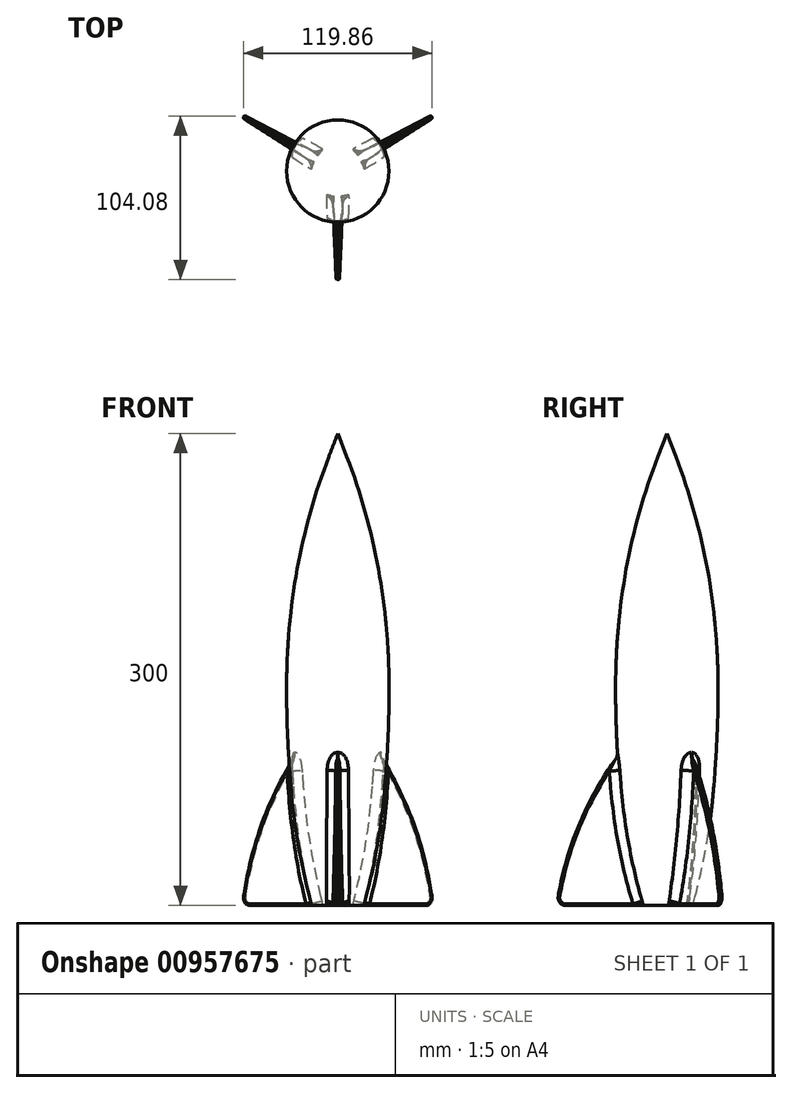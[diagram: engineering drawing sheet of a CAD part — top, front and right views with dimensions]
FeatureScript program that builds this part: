
annotation { "Feature Type Name" : "Feature", "Feature Type Description" : "" }
export const myFeature = defineFeature(function(context is Context, id is Id, definition is map)
    precondition{}
    {
        {
            var Q0;
            Q0=qCreatedBy(makeId("Front.planeOp"),FACE);
            var sketch = newSketch(context, id + "F0", { "sketchPlane" : qUnion([Q0])});
            skLineSegment(sketch, "E0", {"start": v(0, 150) * mm, "end": v(5.68, 135.23) * mm});
            skLineSegment(sketch, "E1", {"start": v(30.36, 31.44) * mm, "end": v(30.51, 29.85) * mm});
            skLineSegment(sketch, "E2", {"start": v(32.5, -9.95) * mm, "end": v(32.5, -14.5) * mm});
            skLineSegment(sketch, "E3", {"start": v(30.5, -65.42) * mm, "end": v(29.8, -74.36) * mm});
            skLineSegment(sketch, "E4", {"start": v(17.92, -144.58) * mm, "end": v(16.5, -150) * mm});
            skLineSegment(sketch, "E5", {"start": v(16.5, -150) * mm, "end": v(0, -150) * mm});
            skLineSegment(sketch, "E6", {"start": v(0, -150) * mm, "end": v(0, 150) * mm});
            skPoint(sketch, "E7.visualSharp", {"position": v(32.5, 10) * mm});
            skArc(sketch, "E7.filletArc", {"start": v(32.5, -9.95) * mm, "mid": v(32, 9.98) * mm, "end": v(30.51, 29.85) * mm});
            skPoint(sketch, "E8.visualSharp", {"position": v(27, -110) * mm});
            skArc(sketch, "E8.filletArc", {"start": v(17.92, -144.58) * mm, "mid": v(25.43, -109.73) * mm, "end": v(29.8, -74.36) * mm});
            skPoint(sketch, "E9.visualSharp", {"position": v(32.5, -40) * mm});
            skArc(sketch, "E9.filletArc", {"start": v(30.5, -65.42) * mm, "mid": v(32, -39.98) * mm, "end": v(32.5, -14.5) * mm});
            skPoint(sketch, "E10.visualSharp", {"position": v(25, 85) * mm});
            skArc(sketch, "E10.filletArc", {"start": v(30.36, 31.44) * mm, "mid": v(21.5, 84.17) * mm, "end": v(5.68, 135.23) * mm});
            skSolve(sketch);
        }
        {
            var Q0;
            Q0=makeQuery(id+"F0.imprint","IMPRINT",FACE,{"disambiguationData":[TD([[makeQuery(id+"F0.imprint","IMPRINT",EDGE,{"derivedFrom":sQuery(id+"F0.wireOp",EDGE,"E0")}),-1.0]])]});
            var Q1;
            Q1=sQuery(id+"F0.wireOp",EDGE,"E6");
            revolve(context, id + "F1", {"surfaceOperationType" : NewSurfaceOperationType.NEW, "entities" : qUnion([Q0]), "axis" : qUnion([Q1]), "revolveType" : RevolveType.FULL});
        }
        {
            var Q0;
            Q0=qCreatedBy(makeId("Top.planeOp"),FACE);
            cPlane(context, id + "F2", {"entities" : qUnion([Q0]), "cplaneType" : CPlaneType.OFFSET, "offset" : 55 * mm, "oppositeDirection" : true, "width" : 150 * mm, "height" : 150 * mm});
        }
        {
            var Q0;
            Q0=qCreatedBy(id+"F2.planeOp",FACE);
            var sketch = newSketch(context, id + "F3", { "sketchPlane" : qUnion([Q0])});
            skLineSegment(sketch, "E11", {"start": v(-1.5, -13) * mm, "end": v(-1, -53) * mm});
            skLineSegment(sketch, "E12", {"start": v(-1, -53) * mm, "end": v(1, -53) * mm});
            skLineSegment(sketch, "E13", {"start": v(1, -53) * mm, "end": v(1.5, -13) * mm});
            skLineSegment(sketch, "E14", {"start": v(1.5, -13) * mm, "end": v(-1.5, -13) * mm});
            skLineSegment(sketch, "E15.1.0", {"start": v(45.4, 27.37) * mm, "end": v(10.5, 7.8) * mm});
            skLineSegment(sketch, "E15.1.1", {"start": v(12, 5.2) * mm, "end": v(46.4, 25.63) * mm});
            skLineSegment(sketch, "E15.1.2", {"start": v(10.5, 7.8) * mm, "end": v(12, 5.2) * mm});
            skLineSegment(sketch, "E15.1.3", {"start": v(46.4, 25.63) * mm, "end": v(45.4, 27.37) * mm});
            skLineSegment(sketch, "E15.2.0", {"start": v(-46.4, 25.63) * mm, "end": v(-12, 5.2) * mm});
            skLineSegment(sketch, "E15.2.1", {"start": v(-10.5, 7.8) * mm, "end": v(-45.4, 27.37) * mm});
            skLineSegment(sketch, "E15.2.2", {"start": v(-12, 5.2) * mm, "end": v(-10.5, 7.8) * mm});
            skLineSegment(sketch, "E15.2.3", {"start": v(-45.4, 27.37) * mm, "end": v(-46.4, 25.63) * mm});
            skPoint(sketch, "E15.center", {"position": v(0, 0) * mm});
            skSolve(sketch);
        }
        {
            var Q0;
            Q0=qCreatedBy(id+"F2.planeOp",FACE);
            cPlane(context, id + "F4", {"entities" : qUnion([Q0]), "cplaneType" : CPlaneType.OFFSET, "offset" : 95 * mm, "oppositeDirection" : true, "width" : 150 * mm, "height" : 150 * mm});
        }
        {
            var Q0;
            Q0=qCreatedBy(id+"F4.planeOp",FACE);
            var sketch = newSketch(context, id + "F5", { "sketchPlane" : qUnion([Q0])});
            skLineSegment(sketch, "E16", {"start": v(-3.5, -13) * mm, "end": v(3.5, -13) * mm});
            skLineSegment(sketch, "E17", {"start": v(3.5, -13) * mm, "end": v(1, -70) * mm});
            skLineSegment(sketch, "E18", {"start": v(1, -70) * mm, "end": v(-1, -70) * mm});
            skLineSegment(sketch, "E19", {"start": v(-1, -70) * mm, "end": v(-3.5, -13) * mm});
            skLineSegment(sketch, "E20.1.0", {"start": v(9.5, 9.53) * mm, "end": v(60.12, 35.87) * mm});
            skLineSegment(sketch, "E20.1.1", {"start": v(61.12, 34.13) * mm, "end": v(13, 3.47) * mm});
            skLineSegment(sketch, "E20.1.2", {"start": v(60.12, 35.87) * mm, "end": v(61.12, 34.13) * mm});
            skLineSegment(sketch, "E20.1.3", {"start": v(13, 3.47) * mm, "end": v(9.5, 9.53) * mm});
            skLineSegment(sketch, "E20.2.0", {"start": v(-13, 3.47) * mm, "end": v(-61.12, 34.13) * mm});
            skLineSegment(sketch, "E20.2.1", {"start": v(-60.12, 35.87) * mm, "end": v(-9.5, 9.53) * mm});
            skLineSegment(sketch, "E20.2.2", {"start": v(-61.12, 34.13) * mm, "end": v(-60.12, 35.87) * mm});
            skLineSegment(sketch, "E20.2.3", {"start": v(-9.5, 9.53) * mm, "end": v(-13, 3.47) * mm});
            skPoint(sketch, "E20.center", {"position": v(0, 0) * mm});
            skSolve(sketch);
        }
        {
            var Q1;
            Q1=makeQuery(id+"F5.imprint","IMPRINT",FACE,{"disambiguationData":[TD([[makeQuery(id+"F5.imprint","IMPRINT",EDGE,{"derivedFrom":sQuery(id+"F5.wireOp",EDGE,"E16")}),-1.0]])]});
            var Q2;
            Q2=makeQuery(id+"F3.imprint","IMPRINT",FACE,{"disambiguationData":[TD([[makeQuery(id+"F3.imprint","IMPRINT",EDGE,{"derivedFrom":sQuery(id+"F3.wireOp",EDGE,"E11")}),1.0]])]});
            loft(context, id + "F6", {"sheetProfilesArray" : [{ "sheetProfileEntities" : qUnion([Q1]) }, { "sheetProfileEntities" : qUnion([Q2]) }]});
        }
        {
            var Q0;
            Q0=qCreatedBy(makeId("Right.planeOp"),FACE);
            var sketch = newSketch(context, id + "F7", { "sketchPlane" : qUnion([Q0])});
            skLineSegment(sketch, "E21", {"start": v(0, 0) * mm, "end": v(0, -150) * mm});
            skSolve(sketch);
        }
        {
            var Q0;
            Q0=makeQuery(id+"F6.opLoft","SWEPT_BODY",BODY,{"disambiguationData":[OSD([makeQuery(id+"F3.imprint","IMPRINT",FACE,{"disambiguationData":[TD([[makeQuery(id+"F3.imprint","IMPRINT",EDGE,{"derivedFrom":sQuery(id+"F3.wireOp",EDGE,"E11")}),1.0]])]}),makeQuery(id+"F5.imprint","IMPRINT",FACE,{"disambiguationData":[TD([[makeQuery(id+"F5.imprint","IMPRINT",EDGE,{"derivedFrom":sQuery(id+"F5.wireOp",EDGE,"E16")}),-1.0]])]})])]});
            var Q1;
            Q1=sQuery(id+"F7.wireOp",EDGE,"E21");
            circularPattern(context, id + "F8", {"entities" : qUnion([Q0]), "axis" : qUnion([Q1]), "angle" : 360 * degree, "instanceCount" : 3, "equalSpace" : true});
        }
        {
            var Q0;
            Q0=makeQuery(id+"F1.opRevolve","SWEPT_BODY",BODY,{"disambiguationData":[OSD([sQuery(id+"F0.wireOp",EDGE,"E0"),sQuery(id+"F0.wireOp",EDGE,"E1"),sQuery(id+"F0.wireOp",EDGE,"E2"),sQuery(id+"F0.wireOp",EDGE,"E3"),sQuery(id+"F0.wireOp",EDGE,"E4"),sQuery(id+"F0.wireOp",EDGE,"E5"),sQuery(id+"F0.wireOp",EDGE,"E6"),sQuery(id+"F0.wireOp",EDGE,"E7.filletArc"),sQuery(id+"F0.wireOp",EDGE,"E8.filletArc"),sQuery(id+"F0.wireOp",EDGE,"E9.filletArc"),sQuery(id+"F0.wireOp",EDGE,"E10.filletArc")])]});
            var Q1;
            Q1=makeQuery(id+"F6.opLoft","SWEPT_BODY",BODY,{"disambiguationData":[OSD([makeQuery(id+"F3.imprint","IMPRINT",FACE,{"disambiguationData":[TD([[makeQuery(id+"F3.imprint","IMPRINT",EDGE,{"derivedFrom":sQuery(id+"F3.wireOp",EDGE,"E11")}),1.0]])]}),makeQuery(id+"F5.imprint","IMPRINT",FACE,{"disambiguationData":[TD([[makeQuery(id+"F5.imprint","IMPRINT",EDGE,{"derivedFrom":sQuery(id+"F5.wireOp",EDGE,"E16")}),-1.0]])]})])]});
            var Q2;
            Q2=makeQuery(id+"F8.opPattern","COPY",BODY,{"derivedFrom":makeQuery(id+"F6.opLoft","SWEPT_BODY",BODY,{"disambiguationData":[OSD([makeQuery(id+"F3.imprint","IMPRINT",FACE,{"disambiguationData":[TD([[makeQuery(id+"F3.imprint","IMPRINT",EDGE,{"derivedFrom":sQuery(id+"F3.wireOp",EDGE,"E11")}),1.0]])]}),makeQuery(id+"F5.imprint","IMPRINT",FACE,{"disambiguationData":[TD([[makeQuery(id+"F5.imprint","IMPRINT",EDGE,{"derivedFrom":sQuery(id+"F5.wireOp",EDGE,"E16")}),-1.0]])]})])]}),"instanceName":"1"});
            var Q3;
            Q3=makeQuery(id+"F8.opPattern","COPY",BODY,{"derivedFrom":makeQuery(id+"F6.opLoft","SWEPT_BODY",BODY,{"disambiguationData":[OSD([makeQuery(id+"F3.imprint","IMPRINT",FACE,{"disambiguationData":[TD([[makeQuery(id+"F3.imprint","IMPRINT",EDGE,{"derivedFrom":sQuery(id+"F3.wireOp",EDGE,"E11")}),1.0]])]}),makeQuery(id+"F5.imprint","IMPRINT",FACE,{"disambiguationData":[TD([[makeQuery(id+"F5.imprint","IMPRINT",EDGE,{"derivedFrom":sQuery(id+"F5.wireOp",EDGE,"E16")}),-1.0]])]})])]}),"instanceName":"2"});
            booleanBodies(context, id + "F9", {"operationType" : BooleanOperationType.UNION, "tools" : qUnion([Q0, Q1, Q2, Q3])});
        }
        {
            var Q0;
            Q0=makeQuery(id+"F6.opLoft","MID_CAP_EDGE",EDGE,{"disambiguationData":[OSD([sQuery(id+"F3.wireOp",EDGE,"E11"),sQuery(id+"F3.wireOp",EDGE,"E12"),sQuery(id+"F3.wireOp",EDGE,"E13")])],"capPos":1.0});
            var Q1;
            Q1=makeQuery(id+"F8.opPattern","COPY",EDGE,{"derivedFrom":makeQuery(id+"F6.opLoft","MID_CAP_EDGE",EDGE,{"disambiguationData":[OSD([sQuery(id+"F3.wireOp",EDGE,"E11"),sQuery(id+"F3.wireOp",EDGE,"E12"),sQuery(id+"F3.wireOp",EDGE,"E13")])],"capPos":1.0}),"instanceName":"1"});
            var Q2;
            Q2=makeQuery(id+"F8.opPattern","COPY",EDGE,{"derivedFrom":makeQuery(id+"F6.opLoft","MID_CAP_EDGE",EDGE,{"disambiguationData":[OSD([sQuery(id+"F3.wireOp",EDGE,"E11"),sQuery(id+"F3.wireOp",EDGE,"E12"),sQuery(id+"F3.wireOp",EDGE,"E13")])],"capPos":1.0}),"instanceName":"2"});
            chamfer(context, id + "F10", {"entities" : qUnion([Q0, Q1, Q2]), "chamferType" : ChamferType.TWO_OFFSETS, "width1" : 22 * mm, "oppositeDirection" : false, "width2" : 35 * mm, "tangentPropagation" : true});
        }
        {
            var Q0;
            {var subQ0=sQuery(id+"F3.wireOp",EDGE,"E13");var subQ1=sQuery(id+"F3.wireOp",EDGE,"E12");var subQ2=sQuery(id+"F3.wireOp",EDGE,"E11");Q0=makeQuery(id+"F10.opChamfer","BLEND_EDGE",EDGE,{"blendedFrom":[makeQuery(id+"F6.opLoft","MID_CAP_EDGE",EDGE,{"disambiguationData":[OSD([subQ2,subQ1,subQ0])],"capPos":1.0}),makeQuery(id+"F6.opLoft","SWEPT_FACE",FACE,{"disambiguationData":[OSD([subQ2,subQ1,subQ0,sQuery(id+"F5.wireOp",EDGE,"E17"),sQuery(id+"F5.wireOp",EDGE,"E18"),sQuery(id+"F5.wireOp",EDGE,"E19")])]})],"blendedInto":[makeQuery(id+"F6.opLoft","SWEPT_FACE",FACE,{"disambiguationData":[OSD([subQ2,subQ1,subQ0,sQuery(id+"F5.wireOp",EDGE,"E17"),sQuery(id+"F5.wireOp",EDGE,"E18"),sQuery(id+"F5.wireOp",EDGE,"E19")])]})]});}
            var Q1;
            {var subQ0=sQuery(id+"F3.wireOp",EDGE,"E13");var subQ1=sQuery(id+"F3.wireOp",EDGE,"E12");var subQ2=sQuery(id+"F3.wireOp",EDGE,"E11");Q1=makeQuery(id+"F10.opChamfer","BLEND_EDGE",EDGE,{"blendedFrom":[makeQuery(id+"F8.opPattern","COPY",EDGE,{"derivedFrom":makeQuery(id+"F6.opLoft","MID_CAP_EDGE",EDGE,{"disambiguationData":[OSD([subQ2,subQ1,subQ0])],"capPos":1.0}),"instanceName":"1"}),makeQuery(id+"F8.opPattern","COPY",FACE,{"derivedFrom":makeQuery(id+"F6.opLoft","SWEPT_FACE",FACE,{"disambiguationData":[OSD([subQ2,subQ1,subQ0,sQuery(id+"F5.wireOp",EDGE,"E17"),sQuery(id+"F5.wireOp",EDGE,"E18"),sQuery(id+"F5.wireOp",EDGE,"E19")])]}),"instanceName":"1"})],"blendedInto":[makeQuery(id+"F8.opPattern","COPY",FACE,{"derivedFrom":makeQuery(id+"F6.opLoft","SWEPT_FACE",FACE,{"disambiguationData":[OSD([subQ2,subQ1,subQ0,sQuery(id+"F5.wireOp",EDGE,"E17"),sQuery(id+"F5.wireOp",EDGE,"E18"),sQuery(id+"F5.wireOp",EDGE,"E19")])]}),"instanceName":"1"})]});}
            var Q2;
            {var subQ0=sQuery(id+"F3.wireOp",EDGE,"E13");var subQ1=sQuery(id+"F3.wireOp",EDGE,"E12");var subQ2=sQuery(id+"F3.wireOp",EDGE,"E11");Q2=makeQuery(id+"F10.opChamfer","BLEND_EDGE",EDGE,{"blendedFrom":[makeQuery(id+"F8.opPattern","COPY",EDGE,{"derivedFrom":makeQuery(id+"F6.opLoft","MID_CAP_EDGE",EDGE,{"disambiguationData":[OSD([subQ2,subQ1,subQ0])],"capPos":1.0}),"instanceName":"2"}),makeQuery(id+"F8.opPattern","COPY",FACE,{"derivedFrom":makeQuery(id+"F6.opLoft","SWEPT_FACE",FACE,{"disambiguationData":[OSD([subQ2,subQ1,subQ0,sQuery(id+"F5.wireOp",EDGE,"E17"),sQuery(id+"F5.wireOp",EDGE,"E18"),sQuery(id+"F5.wireOp",EDGE,"E19")])]}),"instanceName":"2"})],"blendedInto":[makeQuery(id+"F8.opPattern","COPY",FACE,{"derivedFrom":makeQuery(id+"F6.opLoft","SWEPT_FACE",FACE,{"disambiguationData":[OSD([subQ2,subQ1,subQ0,sQuery(id+"F5.wireOp",EDGE,"E17"),sQuery(id+"F5.wireOp",EDGE,"E18"),sQuery(id+"F5.wireOp",EDGE,"E19")])]}),"instanceName":"2"})]});}
            fillet(context, id + "F11", {"entities" : qUnion([Q0, Q1, Q2]), "radius" : 210 * mm, "tangentPropagation" : true, "allowEdgeOverflow" : false});
        }
        {
            var Q0;
            {var subQ0=sQuery(id+"F5.wireOp",EDGE,"E16");var subQ1=sQuery(id+"F5.wireOp",EDGE,"E17");var subQ2=sQuery(id+"F5.wireOp",EDGE,"E18");var subQ5=sQuery(id+"F3.wireOp",EDGE,"E14");var subQ6=sQuery(id+"F3.wireOp",EDGE,"E12");var subQ7=sQuery(id+"F0.wireOp",EDGE,"E5");var subQ8=sQuery(id+"F0.wireOp",EDGE,"E4");Q0=makeQuery(id+"F9.opBoolean","SPLIT",EDGE,{"disambiguationData":[TD([makeQuery(id+"F6.opLoft","SWEPT_FACE",FACE,{"disambiguationData":[OSD([subQ6,sQuery(id+"F3.wireOp",EDGE,"E13"),subQ5,subQ0,subQ1,subQ2])]})])],"derivedFrom":makeQuery(id+"F1.opRevolve","SWEPT_EDGE",EDGE,{"disambiguationData":[OSD([subQ8,subQ7])]})});}
            var Q1;
            {var subQ0=sQuery(id+"F5.wireOp",EDGE,"E16");var subQ2=sQuery(id+"F5.wireOp",EDGE,"E18");var subQ3=sQuery(id+"F5.wireOp",EDGE,"E19");var subQ5=sQuery(id+"F3.wireOp",EDGE,"E14");var subQ6=sQuery(id+"F3.wireOp",EDGE,"E12");var subQ7=sQuery(id+"F0.wireOp",EDGE,"E5");var subQ8=sQuery(id+"F0.wireOp",EDGE,"E4");Q1=makeQuery(id+"F9.opBoolean","SPLIT",EDGE,{"disambiguationData":[TD([makeQuery(id+"F6.opLoft","SWEPT_FACE",FACE,{"disambiguationData":[OSD([sQuery(id+"F3.wireOp",EDGE,"E11"),subQ6,subQ5,subQ0,subQ2,subQ3])]})])],"derivedFrom":makeQuery(id+"F1.opRevolve","SWEPT_EDGE",EDGE,{"disambiguationData":[OSD([subQ8,subQ7])]})});}
            var Q2;
            {var subQ0=sQuery(id+"F5.wireOp",EDGE,"E16");var subQ2=sQuery(id+"F5.wireOp",EDGE,"E18");var subQ3=sQuery(id+"F5.wireOp",EDGE,"E19");var subQ5=sQuery(id+"F0.wireOp",EDGE,"E5");var subQ6=sQuery(id+"F3.wireOp",EDGE,"E14");var subQ7=sQuery(id+"F3.wireOp",EDGE,"E12");var subQ8=sQuery(id+"F0.wireOp",EDGE,"E4");Q2=makeQuery(id+"F9.opBoolean","SPLIT",EDGE,{"disambiguationData":[TD([makeQuery(id+"F8.opPattern","COPY",FACE,{"derivedFrom":makeQuery(id+"F6.opLoft","SWEPT_FACE",FACE,{"disambiguationData":[OSD([sQuery(id+"F3.wireOp",EDGE,"E11"),subQ7,subQ6,subQ0,subQ2,subQ3])]}),"instanceName":"1"})])],"derivedFrom":makeQuery(id+"F1.opRevolve","SWEPT_EDGE",EDGE,{"disambiguationData":[OSD([subQ8,subQ5])]})});}
            fillet(context, id + "F12", {"entities" : qUnion([Q0, Q1, Q2]), "radius" : .5 * mm, "tangentPropagation" : true, "allowEdgeOverflow" : false});
        }
        {
            var Q0;
            Q0=makeQuery(id+"F6.opLoft","MID_CAP_EDGE",EDGE,{"disambiguationData":[OSD([sQuery(id+"F5.wireOp",EDGE,"E17"),sQuery(id+"F5.wireOp",EDGE,"E18"),sQuery(id+"F5.wireOp",EDGE,"E19")])],"capPos":0.0});
            var Q1;
            Q1=makeQuery(id+"F8.opPattern","COPY",EDGE,{"derivedFrom":makeQuery(id+"F6.opLoft","MID_CAP_EDGE",EDGE,{"disambiguationData":[OSD([sQuery(id+"F5.wireOp",EDGE,"E17"),sQuery(id+"F5.wireOp",EDGE,"E18"),sQuery(id+"F5.wireOp",EDGE,"E19")])],"capPos":0.0}),"instanceName":"1"});
            var Q2;
            Q2=makeQuery(id+"F8.opPattern","COPY",EDGE,{"derivedFrom":makeQuery(id+"F6.opLoft","MID_CAP_EDGE",EDGE,{"disambiguationData":[OSD([sQuery(id+"F5.wireOp",EDGE,"E17"),sQuery(id+"F5.wireOp",EDGE,"E18"),sQuery(id+"F5.wireOp",EDGE,"E19")])],"capPos":0.0}),"instanceName":"2"});
            fillet(context, id + "F13", {"entities" : qUnion([Q0, Q1, Q2]), "radius" : 5 * mm, "tangentPropagation" : true, "allowEdgeOverflow" : false});
        }
        {
            var Q0;
            {var subQ0=sQuery(id+"F5.wireOp",EDGE,"E19");var subQ1=sQuery(id+"F5.wireOp",EDGE,"E18");var subQ2=sQuery(id+"F3.wireOp",EDGE,"E12");var subQ3=sQuery(id+"F3.wireOp",EDGE,"E11");var subQ4=sQuery(id+"F3.wireOp",EDGE,"E13");Q0=makeQuery(id+"F11.opFillet","BLEND_EDGE",EDGE,{"blendedFrom":[makeQuery(id+"F10.opChamfer","BLEND_EDGE",EDGE,{"blendedFrom":[makeQuery(id+"F6.opLoft","MID_CAP_EDGE",EDGE,{"disambiguationData":[OSD([subQ3,subQ2,subQ4])],"capPos":1.0}),makeQuery(id+"F6.opLoft","SWEPT_FACE",FACE,{"disambiguationData":[OSD([subQ3,subQ2,subQ4,sQuery(id+"F5.wireOp",EDGE,"E17"),subQ1,subQ0])]})],"blendedInto":[makeQuery(id+"F6.opLoft","SWEPT_FACE",FACE,{"disambiguationData":[OSD([subQ3,subQ2,subQ4,sQuery(id+"F5.wireOp",EDGE,"E17"),subQ1,subQ0])]})]}),makeQuery(id+"F6.opLoft","SWEPT_FACE",FACE,{"disambiguationData":[OSD([subQ3,subQ2,sQuery(id+"F3.wireOp",EDGE,"E14"),sQuery(id+"F5.wireOp",EDGE,"E16"),subQ1,subQ0])]})],"blendedInto":[makeQuery(id+"F6.opLoft","SWEPT_FACE",FACE,{"disambiguationData":[OSD([subQ3,subQ2,sQuery(id+"F3.wireOp",EDGE,"E14"),sQuery(id+"F5.wireOp",EDGE,"E16"),subQ1,subQ0])]})]});}
            var Q1;
            {var subQ0=sQuery(id+"F5.wireOp",EDGE,"E18");var subQ1=sQuery(id+"F5.wireOp",EDGE,"E17");var subQ2=sQuery(id+"F3.wireOp",EDGE,"E13");var subQ3=sQuery(id+"F3.wireOp",EDGE,"E12");var subQ4=sQuery(id+"F3.wireOp",EDGE,"E11");Q1=makeQuery(id+"F11.opFillet","BLEND_EDGE",EDGE,{"blendedFrom":[makeQuery(id+"F10.opChamfer","BLEND_EDGE",EDGE,{"blendedFrom":[makeQuery(id+"F6.opLoft","MID_CAP_EDGE",EDGE,{"disambiguationData":[OSD([subQ4,subQ3,subQ2])],"capPos":1.0}),makeQuery(id+"F6.opLoft","SWEPT_FACE",FACE,{"disambiguationData":[OSD([subQ4,subQ3,subQ2,subQ1,subQ0,sQuery(id+"F5.wireOp",EDGE,"E19")])]})],"blendedInto":[makeQuery(id+"F6.opLoft","SWEPT_FACE",FACE,{"disambiguationData":[OSD([subQ4,subQ3,subQ2,subQ1,subQ0,sQuery(id+"F5.wireOp",EDGE,"E19")])]})]}),makeQuery(id+"F6.opLoft","SWEPT_FACE",FACE,{"disambiguationData":[OSD([subQ3,subQ2,sQuery(id+"F3.wireOp",EDGE,"E14"),sQuery(id+"F5.wireOp",EDGE,"E16"),subQ1,subQ0])]})],"blendedInto":[makeQuery(id+"F6.opLoft","SWEPT_FACE",FACE,{"disambiguationData":[OSD([subQ3,subQ2,sQuery(id+"F3.wireOp",EDGE,"E14"),sQuery(id+"F5.wireOp",EDGE,"E16"),subQ1,subQ0])]})]});}
            var Q2;
            {var subQ0=sQuery(id+"F5.wireOp",EDGE,"E18");var subQ1=sQuery(id+"F5.wireOp",EDGE,"E17");var subQ2=sQuery(id+"F3.wireOp",EDGE,"E13");var subQ3=sQuery(id+"F3.wireOp",EDGE,"E12");var subQ4=sQuery(id+"F3.wireOp",EDGE,"E11");Q2=makeQuery(id+"F11.opFillet","BLEND_EDGE",EDGE,{"blendedFrom":[makeQuery(id+"F10.opChamfer","BLEND_EDGE",EDGE,{"blendedFrom":[makeQuery(id+"F8.opPattern","COPY",EDGE,{"derivedFrom":makeQuery(id+"F6.opLoft","MID_CAP_EDGE",EDGE,{"disambiguationData":[OSD([subQ4,subQ3,subQ2])],"capPos":1.0}),"instanceName":"1"}),makeQuery(id+"F8.opPattern","COPY",FACE,{"derivedFrom":makeQuery(id+"F6.opLoft","SWEPT_FACE",FACE,{"disambiguationData":[OSD([subQ4,subQ3,subQ2,subQ1,subQ0,sQuery(id+"F5.wireOp",EDGE,"E19")])]}),"instanceName":"1"})],"blendedInto":[makeQuery(id+"F8.opPattern","COPY",FACE,{"derivedFrom":makeQuery(id+"F6.opLoft","SWEPT_FACE",FACE,{"disambiguationData":[OSD([subQ4,subQ3,subQ2,subQ1,subQ0,sQuery(id+"F5.wireOp",EDGE,"E19")])]}),"instanceName":"1"})]}),makeQuery(id+"F8.opPattern","COPY",FACE,{"derivedFrom":makeQuery(id+"F6.opLoft","SWEPT_FACE",FACE,{"disambiguationData":[OSD([subQ3,subQ2,sQuery(id+"F3.wireOp",EDGE,"E14"),sQuery(id+"F5.wireOp",EDGE,"E16"),subQ1,subQ0])]}),"instanceName":"1"})],"blendedInto":[makeQuery(id+"F8.opPattern","COPY",FACE,{"derivedFrom":makeQuery(id+"F6.opLoft","SWEPT_FACE",FACE,{"disambiguationData":[OSD([subQ3,subQ2,sQuery(id+"F3.wireOp",EDGE,"E14"),sQuery(id+"F5.wireOp",EDGE,"E16"),subQ1,subQ0])]}),"instanceName":"1"})]});}
            var Q3;
            {var subQ0=sQuery(id+"F5.wireOp",EDGE,"E19");var subQ1=sQuery(id+"F5.wireOp",EDGE,"E18");var subQ2=sQuery(id+"F3.wireOp",EDGE,"E12");var subQ3=sQuery(id+"F3.wireOp",EDGE,"E11");var subQ4=sQuery(id+"F3.wireOp",EDGE,"E13");Q3=makeQuery(id+"F11.opFillet","BLEND_EDGE",EDGE,{"blendedFrom":[makeQuery(id+"F10.opChamfer","BLEND_EDGE",EDGE,{"blendedFrom":[makeQuery(id+"F8.opPattern","COPY",EDGE,{"derivedFrom":makeQuery(id+"F6.opLoft","MID_CAP_EDGE",EDGE,{"disambiguationData":[OSD([subQ3,subQ2,subQ4])],"capPos":1.0}),"instanceName":"1"}),makeQuery(id+"F8.opPattern","COPY",FACE,{"derivedFrom":makeQuery(id+"F6.opLoft","SWEPT_FACE",FACE,{"disambiguationData":[OSD([subQ3,subQ2,subQ4,sQuery(id+"F5.wireOp",EDGE,"E17"),subQ1,subQ0])]}),"instanceName":"1"})],"blendedInto":[makeQuery(id+"F8.opPattern","COPY",FACE,{"derivedFrom":makeQuery(id+"F6.opLoft","SWEPT_FACE",FACE,{"disambiguationData":[OSD([subQ3,subQ2,subQ4,sQuery(id+"F5.wireOp",EDGE,"E17"),subQ1,subQ0])]}),"instanceName":"1"})]}),makeQuery(id+"F8.opPattern","COPY",FACE,{"derivedFrom":makeQuery(id+"F6.opLoft","SWEPT_FACE",FACE,{"disambiguationData":[OSD([subQ3,subQ2,sQuery(id+"F3.wireOp",EDGE,"E14"),sQuery(id+"F5.wireOp",EDGE,"E16"),subQ1,subQ0])]}),"instanceName":"1"})],"blendedInto":[makeQuery(id+"F8.opPattern","COPY",FACE,{"derivedFrom":makeQuery(id+"F6.opLoft","SWEPT_FACE",FACE,{"disambiguationData":[OSD([subQ3,subQ2,sQuery(id+"F3.wireOp",EDGE,"E14"),sQuery(id+"F5.wireOp",EDGE,"E16"),subQ1,subQ0])]}),"instanceName":"1"})]});}
            var Q4;
            {var subQ0=sQuery(id+"F5.wireOp",EDGE,"E18");var subQ1=sQuery(id+"F5.wireOp",EDGE,"E17");var subQ2=sQuery(id+"F3.wireOp",EDGE,"E13");var subQ3=sQuery(id+"F3.wireOp",EDGE,"E12");var subQ4=sQuery(id+"F3.wireOp",EDGE,"E11");Q4=makeQuery(id+"F11.opFillet","BLEND_EDGE",EDGE,{"blendedFrom":[makeQuery(id+"F10.opChamfer","BLEND_EDGE",EDGE,{"blendedFrom":[makeQuery(id+"F8.opPattern","COPY",EDGE,{"derivedFrom":makeQuery(id+"F6.opLoft","MID_CAP_EDGE",EDGE,{"disambiguationData":[OSD([subQ4,subQ3,subQ2])],"capPos":1.0}),"instanceName":"2"}),makeQuery(id+"F8.opPattern","COPY",FACE,{"derivedFrom":makeQuery(id+"F6.opLoft","SWEPT_FACE",FACE,{"disambiguationData":[OSD([subQ4,subQ3,subQ2,subQ1,subQ0,sQuery(id+"F5.wireOp",EDGE,"E19")])]}),"instanceName":"2"})],"blendedInto":[makeQuery(id+"F8.opPattern","COPY",FACE,{"derivedFrom":makeQuery(id+"F6.opLoft","SWEPT_FACE",FACE,{"disambiguationData":[OSD([subQ4,subQ3,subQ2,subQ1,subQ0,sQuery(id+"F5.wireOp",EDGE,"E19")])]}),"instanceName":"2"})]}),makeQuery(id+"F8.opPattern","COPY",FACE,{"derivedFrom":makeQuery(id+"F6.opLoft","SWEPT_FACE",FACE,{"disambiguationData":[OSD([subQ3,subQ2,sQuery(id+"F3.wireOp",EDGE,"E14"),sQuery(id+"F5.wireOp",EDGE,"E16"),subQ1,subQ0])]}),"instanceName":"2"})],"blendedInto":[makeQuery(id+"F8.opPattern","COPY",FACE,{"derivedFrom":makeQuery(id+"F6.opLoft","SWEPT_FACE",FACE,{"disambiguationData":[OSD([subQ3,subQ2,sQuery(id+"F3.wireOp",EDGE,"E14"),sQuery(id+"F5.wireOp",EDGE,"E16"),subQ1,subQ0])]}),"instanceName":"2"})]});}
            var Q5;
            {var subQ0=sQuery(id+"F5.wireOp",EDGE,"E19");var subQ1=sQuery(id+"F5.wireOp",EDGE,"E18");var subQ2=sQuery(id+"F3.wireOp",EDGE,"E12");var subQ3=sQuery(id+"F3.wireOp",EDGE,"E11");var subQ4=sQuery(id+"F3.wireOp",EDGE,"E13");Q5=makeQuery(id+"F11.opFillet","BLEND_EDGE",EDGE,{"blendedFrom":[makeQuery(id+"F10.opChamfer","BLEND_EDGE",EDGE,{"blendedFrom":[makeQuery(id+"F8.opPattern","COPY",EDGE,{"derivedFrom":makeQuery(id+"F6.opLoft","MID_CAP_EDGE",EDGE,{"disambiguationData":[OSD([subQ3,subQ2,subQ4])],"capPos":1.0}),"instanceName":"2"}),makeQuery(id+"F8.opPattern","COPY",FACE,{"derivedFrom":makeQuery(id+"F6.opLoft","SWEPT_FACE",FACE,{"disambiguationData":[OSD([subQ3,subQ2,subQ4,sQuery(id+"F5.wireOp",EDGE,"E17"),subQ1,subQ0])]}),"instanceName":"2"})],"blendedInto":[makeQuery(id+"F8.opPattern","COPY",FACE,{"derivedFrom":makeQuery(id+"F6.opLoft","SWEPT_FACE",FACE,{"disambiguationData":[OSD([subQ3,subQ2,subQ4,sQuery(id+"F5.wireOp",EDGE,"E17"),subQ1,subQ0])]}),"instanceName":"2"})]}),makeQuery(id+"F8.opPattern","COPY",FACE,{"derivedFrom":makeQuery(id+"F6.opLoft","SWEPT_FACE",FACE,{"disambiguationData":[OSD([subQ3,subQ2,sQuery(id+"F3.wireOp",EDGE,"E14"),sQuery(id+"F5.wireOp",EDGE,"E16"),subQ1,subQ0])]}),"instanceName":"2"})],"blendedInto":[makeQuery(id+"F8.opPattern","COPY",FACE,{"derivedFrom":makeQuery(id+"F6.opLoft","SWEPT_FACE",FACE,{"disambiguationData":[OSD([subQ3,subQ2,sQuery(id+"F3.wireOp",EDGE,"E14"),sQuery(id+"F5.wireOp",EDGE,"E16"),subQ1,subQ0])]}),"instanceName":"2"})]});}
            fillet(context, id + "F14", {"entities" : qUnion([Q0, Q1, Q2, Q3, Q4, Q5]), "radius" : 1 * mm, "tangentPropagation" : true, "allowEdgeOverflow" : false});
        }
        {
            var Q0;
            {var subQ0=sQuery(id+"F5.wireOp",EDGE,"E18");var subQ1=sQuery(id+"F5.wireOp",EDGE,"E17");var subQ2=sQuery(id+"F3.wireOp",EDGE,"E13");var subQ3=sQuery(id+"F3.wireOp",EDGE,"E12");var subQ4=sQuery(id+"F3.wireOp",EDGE,"E11");Q0=makeQuery(id+"F14.opFillet","BLEND_EDGE",EDGE,{"blendedFrom":[makeQuery(id+"F11.opFillet","BLEND_EDGE",EDGE,{"blendedFrom":[makeQuery(id+"F10.opChamfer","BLEND_EDGE",EDGE,{"blendedFrom":[makeQuery(id+"F6.opLoft","MID_CAP_EDGE",EDGE,{"disambiguationData":[OSD([subQ4,subQ3,subQ2])],"capPos":1.0}),makeQuery(id+"F6.opLoft","SWEPT_FACE",FACE,{"disambiguationData":[OSD([subQ4,subQ3,subQ2,subQ1,subQ0,sQuery(id+"F5.wireOp",EDGE,"E19")])]})],"blendedInto":[makeQuery(id+"F6.opLoft","SWEPT_FACE",FACE,{"disambiguationData":[OSD([subQ4,subQ3,subQ2,subQ1,subQ0,sQuery(id+"F5.wireOp",EDGE,"E19")])]})]}),makeQuery(id+"F6.opLoft","SWEPT_FACE",FACE,{"disambiguationData":[OSD([subQ3,subQ2,sQuery(id+"F3.wireOp",EDGE,"E14"),sQuery(id+"F5.wireOp",EDGE,"E16"),subQ1,subQ0])]})],"blendedInto":[makeQuery(id+"F6.opLoft","SWEPT_FACE",FACE,{"disambiguationData":[OSD([subQ3,subQ2,sQuery(id+"F3.wireOp",EDGE,"E14"),sQuery(id+"F5.wireOp",EDGE,"E16"),subQ1,subQ0])]})]}),makeQuery(id+"F1.opRevolve","SWEPT_FACE",FACE,{"disambiguationData":[OSD([sQuery(id+"F0.wireOp",EDGE,"E9.filletArc")])]})],"blendedInto":[makeQuery(id+"F1.opRevolve","SWEPT_FACE",FACE,{"disambiguationData":[OSD([sQuery(id+"F0.wireOp",EDGE,"E9.filletArc")])]})]});}
            var Q1;
            {var subQ0=sQuery(id+"F5.wireOp",EDGE,"E18");var subQ1=sQuery(id+"F5.wireOp",EDGE,"E17");var subQ2=sQuery(id+"F3.wireOp",EDGE,"E13");var subQ3=sQuery(id+"F3.wireOp",EDGE,"E12");var subQ4=sQuery(id+"F3.wireOp",EDGE,"E11");Q1=makeQuery(id+"F14.opFillet","BLEND_EDGE",EDGE,{"blendedFrom":[makeQuery(id+"F11.opFillet","BLEND_EDGE",EDGE,{"blendedFrom":[makeQuery(id+"F10.opChamfer","BLEND_EDGE",EDGE,{"blendedFrom":[makeQuery(id+"F8.opPattern","COPY",EDGE,{"derivedFrom":makeQuery(id+"F6.opLoft","MID_CAP_EDGE",EDGE,{"disambiguationData":[OSD([subQ4,subQ3,subQ2])],"capPos":1.0}),"instanceName":"1"}),makeQuery(id+"F8.opPattern","COPY",FACE,{"derivedFrom":makeQuery(id+"F6.opLoft","SWEPT_FACE",FACE,{"disambiguationData":[OSD([subQ4,subQ3,subQ2,subQ1,subQ0,sQuery(id+"F5.wireOp",EDGE,"E19")])]}),"instanceName":"1"})],"blendedInto":[makeQuery(id+"F8.opPattern","COPY",FACE,{"derivedFrom":makeQuery(id+"F6.opLoft","SWEPT_FACE",FACE,{"disambiguationData":[OSD([subQ4,subQ3,subQ2,subQ1,subQ0,sQuery(id+"F5.wireOp",EDGE,"E19")])]}),"instanceName":"1"})]}),makeQuery(id+"F8.opPattern","COPY",FACE,{"derivedFrom":makeQuery(id+"F6.opLoft","SWEPT_FACE",FACE,{"disambiguationData":[OSD([subQ3,subQ2,sQuery(id+"F3.wireOp",EDGE,"E14"),sQuery(id+"F5.wireOp",EDGE,"E16"),subQ1,subQ0])]}),"instanceName":"1"})],"blendedInto":[makeQuery(id+"F8.opPattern","COPY",FACE,{"derivedFrom":makeQuery(id+"F6.opLoft","SWEPT_FACE",FACE,{"disambiguationData":[OSD([subQ3,subQ2,sQuery(id+"F3.wireOp",EDGE,"E14"),sQuery(id+"F5.wireOp",EDGE,"E16"),subQ1,subQ0])]}),"instanceName":"1"})]}),makeQuery(id+"F1.opRevolve","SWEPT_FACE",FACE,{"disambiguationData":[OSD([sQuery(id+"F0.wireOp",EDGE,"E9.filletArc")])]})],"blendedInto":[makeQuery(id+"F1.opRevolve","SWEPT_FACE",FACE,{"disambiguationData":[OSD([sQuery(id+"F0.wireOp",EDGE,"E9.filletArc")])]})]});}
            var Q2;
            {var subQ0=sQuery(id+"F5.wireOp",EDGE,"E18");var subQ1=sQuery(id+"F5.wireOp",EDGE,"E17");var subQ2=sQuery(id+"F3.wireOp",EDGE,"E13");var subQ3=sQuery(id+"F3.wireOp",EDGE,"E12");var subQ4=sQuery(id+"F3.wireOp",EDGE,"E11");Q2=makeQuery(id+"F14.opFillet","BLEND_EDGE",EDGE,{"blendedFrom":[makeQuery(id+"F11.opFillet","BLEND_EDGE",EDGE,{"blendedFrom":[makeQuery(id+"F10.opChamfer","BLEND_EDGE",EDGE,{"blendedFrom":[makeQuery(id+"F8.opPattern","COPY",EDGE,{"derivedFrom":makeQuery(id+"F6.opLoft","MID_CAP_EDGE",EDGE,{"disambiguationData":[OSD([subQ4,subQ3,subQ2])],"capPos":1.0}),"instanceName":"2"}),makeQuery(id+"F8.opPattern","COPY",FACE,{"derivedFrom":makeQuery(id+"F6.opLoft","SWEPT_FACE",FACE,{"disambiguationData":[OSD([subQ4,subQ3,subQ2,subQ1,subQ0,sQuery(id+"F5.wireOp",EDGE,"E19")])]}),"instanceName":"2"})],"blendedInto":[makeQuery(id+"F8.opPattern","COPY",FACE,{"derivedFrom":makeQuery(id+"F6.opLoft","SWEPT_FACE",FACE,{"disambiguationData":[OSD([subQ4,subQ3,subQ2,subQ1,subQ0,sQuery(id+"F5.wireOp",EDGE,"E19")])]}),"instanceName":"2"})]}),makeQuery(id+"F8.opPattern","COPY",FACE,{"derivedFrom":makeQuery(id+"F6.opLoft","SWEPT_FACE",FACE,{"disambiguationData":[OSD([subQ3,subQ2,sQuery(id+"F3.wireOp",EDGE,"E14"),sQuery(id+"F5.wireOp",EDGE,"E16"),subQ1,subQ0])]}),"instanceName":"2"})],"blendedInto":[makeQuery(id+"F8.opPattern","COPY",FACE,{"derivedFrom":makeQuery(id+"F6.opLoft","SWEPT_FACE",FACE,{"disambiguationData":[OSD([subQ3,subQ2,sQuery(id+"F3.wireOp",EDGE,"E14"),sQuery(id+"F5.wireOp",EDGE,"E16"),subQ1,subQ0])]}),"instanceName":"2"})]}),makeQuery(id+"F1.opRevolve","SWEPT_FACE",FACE,{"disambiguationData":[OSD([sQuery(id+"F0.wireOp",EDGE,"E9.filletArc")])]})],"blendedInto":[makeQuery(id+"F1.opRevolve","SWEPT_FACE",FACE,{"disambiguationData":[OSD([sQuery(id+"F0.wireOp",EDGE,"E9.filletArc")])]})]});}
            fillet(context, id + "F15", {"entities" : qUnion([Q0, Q1, Q2]), "radius" : 7 * mm, "tangentPropagation" : true, "allowEdgeOverflow" : false});
        }
    });
